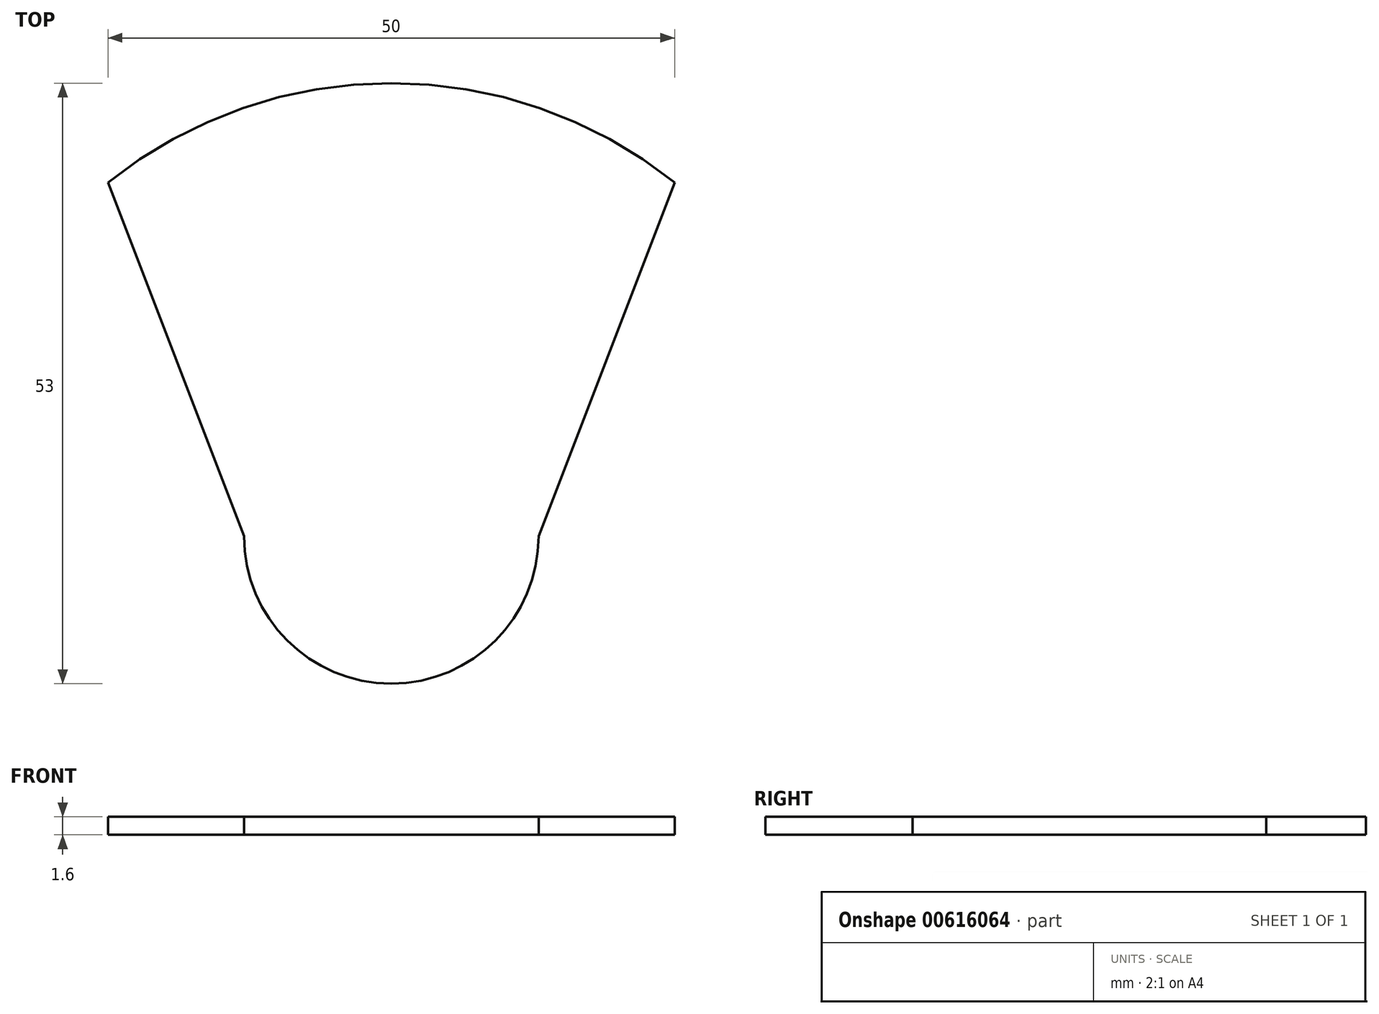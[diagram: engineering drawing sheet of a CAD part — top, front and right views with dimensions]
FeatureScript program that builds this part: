
annotation { "Feature Type Name" : "Feature", "Feature Type Description" : "" }
export const myFeature = defineFeature(function(context is Context, id is Id, definition is map)
    precondition{}
    {
        {
            var Q0;
            Q0=qCreatedBy(makeId("Top.planeOp"),FACE);
            var sketch = newSketch(context, id + "F0", { "sketchPlane" : qUnion([Q0])});
            skArc(sketch, "E0", {"start": v(-13, 0) * mm, "mid": v(0, -13) * mm, "end": v(13, 0) * mm});
            skArc(sketch, "E1", {"start": v(25, 31.22) * mm, "mid": v(0, 40) * mm, "end": v(-25, 31.22) * mm});
            skLineSegment(sketch, "E2", {"start": v(-25, 31.22) * mm, "end": v(-13, 0) * mm});
            skLineSegment(sketch, "E3", {"start": v(13, 0) * mm, "end": v(25, 31.22) * mm});
            skSolve(sketch);
        }
        {
            var Q0;
            Q0 = qSketchRegion(id + "F0", true);
            extrude(context, id + "F1", {"entities" : qUnion([Q0]), "depth" : 1.6 * mm, "offsetDistance" : 25 * mm});
        }
    });
